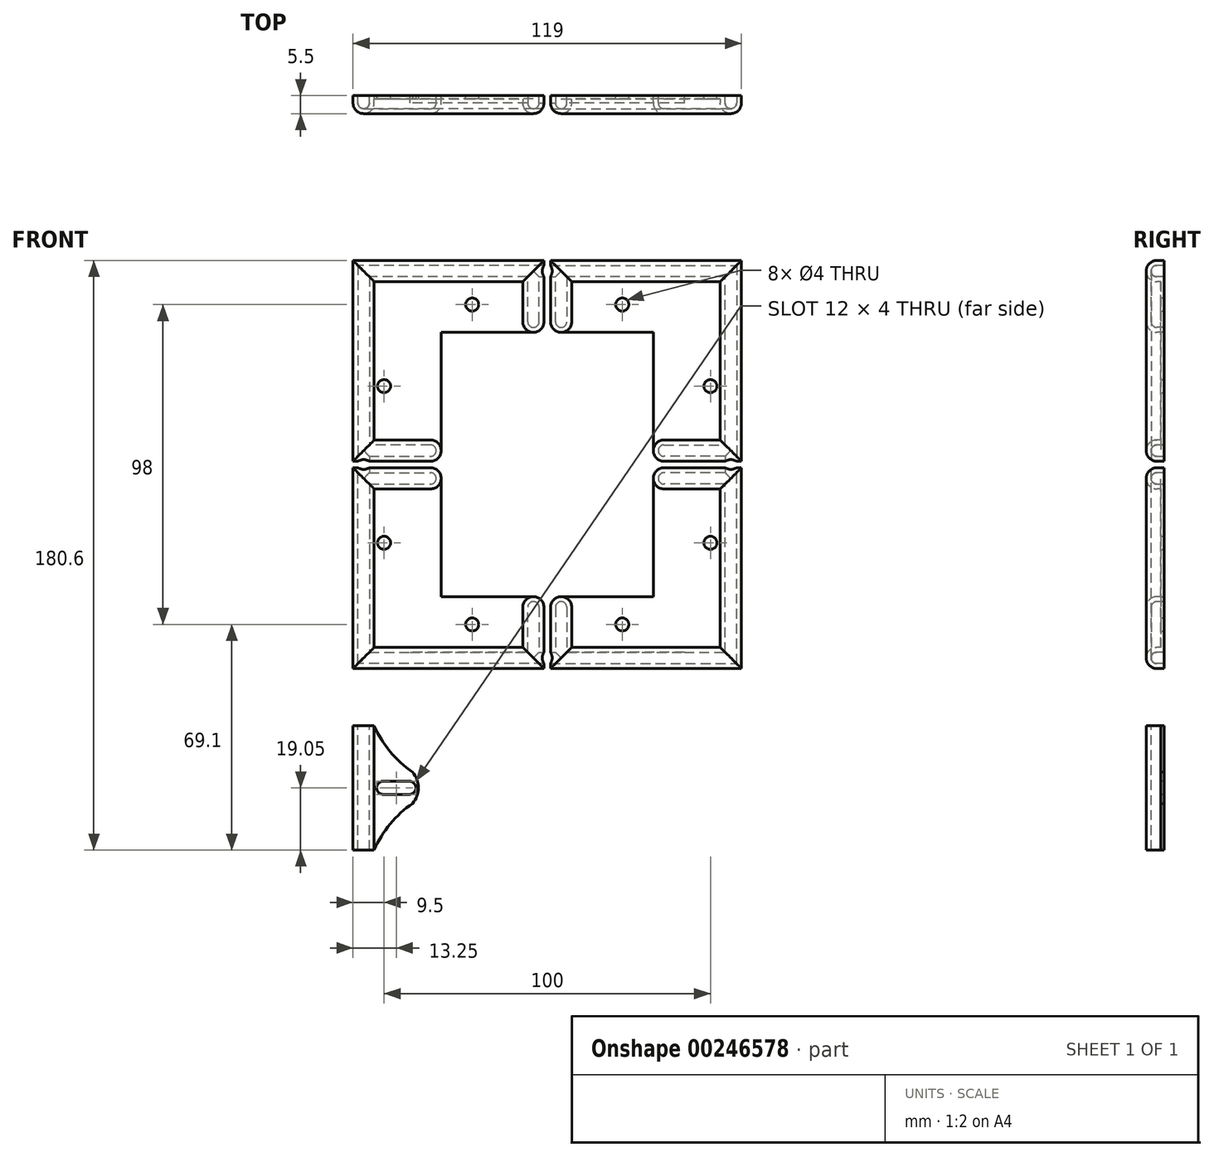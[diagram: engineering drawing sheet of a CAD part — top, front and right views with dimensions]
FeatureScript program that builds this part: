
annotation { "Feature Type Name" : "Feature", "Feature Type Description" : "" }
export const myFeature = defineFeature(function(context is Context, id is Id, definition is map)
    precondition{}
    {
        {
            var Q0;
            Q0=qCreatedBy(makeId("Front.planeOp"),FACE);
            var sketch = newSketch(context, id + "F0", { "sketchPlane" : qUnion([Q0])});
            skLineSegment(sketch, "E0", {"start": v(59.5, 0) * mm, "end": v(59.5, 61.5) * mm});
            skLineSegment(sketch, "E1", {"start": v(59.5, 61.5) * mm, "end": v(1, 61.5) * mm});
            skLineSegment(sketch, "E2", {"start": v(1, 61.5) * mm, "end": v(1, 39.5) * mm});
            skLineSegment(sketch, "E3", {"start": v(1, 39.5) * mm, "end": v(32.5, 39.5) * mm});
            skLineSegment(sketch, "E4", {"start": v(32.5, 39.5) * mm, "end": v(32.5, 0) * mm});
            skLineSegment(sketch, "E5", {"start": v(32.5, 0) * mm, "end": v(59.5, 0) * mm});
            skCircle(sketch, "E6", {"center": v(23, 48) * mm, "radius": 2 * mm});
            skCircle(sketch, "E7", {"center": v(50, 23) * mm, "radius": 2 * mm});
            skSolve(sketch);
        }
        {
            var Q0;
            Q0=qCreatedBy(makeId("Right.planeOp"),FACE);
            var sketch = newSketch(context, id + "F1", { "sketchPlane" : qUnion([Q0])});
            skArc(sketch, "E8", {"start": v(-2.25, 61.5) * mm, "mid": v(-5.5, 58.25) * mm, "end": v(-2.25, 55) * mm});
            skLineSegment(sketch, "E9", {"start": v(0, 61.5) * mm, "end": v(-2.25, 61.5) * mm});
            skLineSegment(sketch, "E10", {"start": v(-2.25, 55) * mm, "end": v(0, 55) * mm});
            skPoint(sketch, "E11", {"position": v(-5.5, 58.25) * mm});
            skLineSegment(sketch, "E12", {"start": v(0, 55) * mm, "end": v(0, 61.5) * mm});
            skSolve(sketch);
        }
        {
            var Q0;
            Q0=qCreatedBy(makeId("Top.planeOp"),FACE);
            cPlane(context, id + "F2", {"entities" : qUnion([Q0]), "cplaneType" : CPlaneType.OFFSET, "offset" : 39.5 * mm, "width" : 150 * mm, "height" : 150 * mm});
        }
        {
            var Q0;
            Q0=qCreatedBy(id+"F2.planeOp",FACE);
            var sketch = newSketch(context, id + "F3", { "sketchPlane" : qUnion([Q0])});
            skArc(sketch, "E13", {"start": v(1, -2.25) * mm, "mid": v(4.25, -5.5) * mm, "end": v(7.5, -2.25) * mm});
            skPoint(sketch, "E14", {"position": v(4.25, -5.5) * mm});
            skPoint(sketch, "E15", {"position": v(1, -2.25) * mm});
            skLineSegment(sketch, "E16", {"start": v(1, 0) * mm, "end": v(7.5, 0) * mm});
            skLineSegment(sketch, "E17", {"start": v(7.5, -2.25) * mm, "end": v(7.5, 0) * mm});
            skLineSegment(sketch, "E18", {"start": v(1, -2.25) * mm, "end": v(1, 0) * mm});
            skSolve(sketch);
        }
        {
            var Q0;
            Q0=makeQuery(id+"F3.imprint","IMPRINT",FACE,{"disambiguationData":[TD([[makeQuery(id+"F3.imprint","IMPRINT",EDGE,{"derivedFrom":sQuery(id+"F3.wireOp",EDGE,"E13")}),1.0]])]});
            var Q1;
            Q1=sQuery(id+"F0.wireOp",EDGE,"E2");
            var Q2;
            Q2=sQuery(id+"F0.wireOp",EDGE,"E1");
            var Q3;
            Q3=sQuery(id+"F0.wireOp",EDGE,"E0");
            var Q4;
            Q4=sQuery(id+"F0.wireOp",EDGE,"E5");
            sweep(context, id + "F4", {"profiles" : qUnion([Q0]), "path" : qUnion([Q1, Q2, Q3, Q4])});
        }
        {
            var Q0;
            Q0=qSketchRegion(id+"F0",true);
            extrude(context, id + "F5", {"entities" : qUnion([Q0]), "operationType" : NewBodyOperationType.ADD, "depth" : 1 * mm});
        }
        {
            var Q0;
            Q0=makeQuery(id+"F4.opSweep","CAP_EDGE",EDGE,{"disambiguationData":[OSD([sQuery(id+"F0.wireOp",VERTEX,"E2.end"),sQuery(id+"F3.wireOp",EDGE,"E13")])],"isStart":true});
            var Q1;
            Q1=makeQuery(id+"F4.opSweep","CAP_EDGE",EDGE,{"disambiguationData":[OSD([sQuery(id+"F0.wireOp",VERTEX,"E5.start"),sQuery(id+"F3.wireOp",EDGE,"E13")])],"isStart":false});
            fillet(context, id + "F6", {"entities" : qUnion([Q0, Q1]), "radius" : 3.25 * mm, "tangentPropagation" : true, "allowEdgeOverflow" : false});
        }
        {
            var Q0;
            Q0=makeQuery(id+"F4.opSweep","SWEPT_BODY",BODY,{"disambiguationData":[OSD([sQuery(id+"F0.wireOp",EDGE,"E5"),sQuery(id+"F3.wireOp",EDGE,"E13"),sQuery(id+"F3.wireOp",EDGE,"gyNzIB6L-VOB3-YhDV-Oq0C-YqyF9qzvM0NL"),sQuery(id+"F3.wireOp",EDGE,"E16"),sQuery(id+"F3.wireOp",EDGE,"E17")])]});
            var Q1;
            Q1=qCreatedBy(makeId("Right.planeOp"),FACE);
            mirror(context, id + "F7", {"entities" : qUnion([Q0]), "mirrorPlane" : qUnion([Q1])});
        }
        {
            var Q0;
            Q0=qCreatedBy(makeId("Top.planeOp"),FACE);
            cPlane(context, id + "F8", {"entities" : qUnion([Q0]), "cplaneType" : CPlaneType.OFFSET, "offset" : 1 * mm, "oppositeDirection" : true, "width" : 150 * mm, "height" : 150 * mm});
        }
        {
            var Q0;
            Q0=makeQuery(id+"F4.opSweep","SWEPT_BODY",BODY,{"disambiguationData":[OSD([sQuery(id+"F0.wireOp",EDGE,"E5"),sQuery(id+"F3.wireOp",EDGE,"E13"),sQuery(id+"F3.wireOp",EDGE,"E16"),sQuery(id+"F3.wireOp",EDGE,"E17"),sQuery(id+"F3.wireOp",EDGE,"E18")])]});
            var Q1;
            Q1=makeQuery(id+"F7.opPattern","COPY",BODY,{"derivedFrom":makeQuery(id+"F4.opSweep","SWEPT_BODY",BODY,{"disambiguationData":[OSD([sQuery(id+"F0.wireOp",EDGE,"E5"),sQuery(id+"F3.wireOp",EDGE,"E13"),sQuery(id+"F3.wireOp",EDGE,"E16"),sQuery(id+"F3.wireOp",EDGE,"E17"),sQuery(id+"F3.wireOp",EDGE,"E18")])]}),"instanceName":"1"});
            var Q2;
            Q2=qCreatedBy(id+"F8.planeOp",FACE);
            mirror(context, id + "F9", {"entities" : qUnion([Q0, Q1]), "mirrorPlane" : qUnion([Q2])});
        }
        {
            var Q0;
            {var subQ0=sQuery(id+"F0.wireOp",EDGE,"E2");Q0=makeQuery(id+"F7.opPattern","COPY",FACE,{"derivedFrom":makeQuery(id+"F5.boolean.opBoolean","MERGE",FACE,{"derivedFrom":[makeQuery(id+"F4.opSweep","SWEPT_FACE",FACE,{"disambiguationData":[OSD([subQ0,sQuery(id+"F3.wireOp",EDGE,"E16")])]}),makeQuery(id+"F5.opExtrude","CAP_FACE",FACE,{"disambiguationData":[OSD([sQuery(id+"F0.wireOp",EDGE,"E0"),sQuery(id+"F0.wireOp",EDGE,"E1"),subQ0,sQuery(id+"F0.wireOp",EDGE,"E3"),sQuery(id+"F0.wireOp",EDGE,"E4"),sQuery(id+"F0.wireOp",EDGE,"E5"),sQuery(id+"F0.wireOp",EDGE,"E6"),sQuery(id+"F0.wireOp",EDGE,"E7")])],"isStart":true})]}),"instanceName":"1"});}
            var Q1;
            {var subQ0=sQuery(id+"F0.wireOp",EDGE,"E2");Q1=makeQuery(id+"F9.opPattern","COPY",FACE,{"derivedFrom":makeQuery(id+"F7.opPattern","COPY",FACE,{"derivedFrom":makeQuery(id+"F5.boolean.opBoolean","MERGE",FACE,{"derivedFrom":[makeQuery(id+"F4.opSweep","SWEPT_FACE",FACE,{"disambiguationData":[OSD([subQ0,sQuery(id+"F3.wireOp",EDGE,"E16")])]}),makeQuery(id+"F5.opExtrude","CAP_FACE",FACE,{"disambiguationData":[OSD([sQuery(id+"F0.wireOp",EDGE,"E0"),sQuery(id+"F0.wireOp",EDGE,"E1"),subQ0,sQuery(id+"F0.wireOp",EDGE,"E3"),sQuery(id+"F0.wireOp",EDGE,"E4"),sQuery(id+"F0.wireOp",EDGE,"E5"),sQuery(id+"F0.wireOp",EDGE,"E6"),sQuery(id+"F0.wireOp",EDGE,"E7")])],"isStart":true})]}),"instanceName":"1"}),"instanceName":"1"});}
            var Q2;
            {var subQ0=sQuery(id+"F0.wireOp",EDGE,"E2");Q2=makeQuery(id+"F9.opPattern","COPY",FACE,{"derivedFrom":makeQuery(id+"F5.boolean.opBoolean","MERGE",FACE,{"derivedFrom":[makeQuery(id+"F4.opSweep","SWEPT_FACE",FACE,{"disambiguationData":[OSD([subQ0,sQuery(id+"F3.wireOp",EDGE,"E16")])]}),makeQuery(id+"F5.opExtrude","CAP_FACE",FACE,{"disambiguationData":[OSD([sQuery(id+"F0.wireOp",EDGE,"E0"),sQuery(id+"F0.wireOp",EDGE,"E1"),subQ0,sQuery(id+"F0.wireOp",EDGE,"E3"),sQuery(id+"F0.wireOp",EDGE,"E4"),sQuery(id+"F0.wireOp",EDGE,"E5"),sQuery(id+"F0.wireOp",EDGE,"E6"),sQuery(id+"F0.wireOp",EDGE,"E7")])],"isStart":true})]}),"instanceName":"1"});}
            var Q3;
            {var subQ0=sQuery(id+"F0.wireOp",EDGE,"E2");Q3=makeQuery(id+"F5.boolean.opBoolean","MERGE",FACE,{"derivedFrom":[makeQuery(id+"F4.opSweep","SWEPT_FACE",FACE,{"disambiguationData":[OSD([subQ0,sQuery(id+"F3.wireOp",EDGE,"E16")])]}),makeQuery(id+"F5.opExtrude","CAP_FACE",FACE,{"disambiguationData":[OSD([sQuery(id+"F0.wireOp",EDGE,"E0"),sQuery(id+"F0.wireOp",EDGE,"E1"),subQ0,sQuery(id+"F0.wireOp",EDGE,"E3"),sQuery(id+"F0.wireOp",EDGE,"E4"),sQuery(id+"F0.wireOp",EDGE,"E5"),sQuery(id+"F0.wireOp",EDGE,"E6"),sQuery(id+"F0.wireOp",EDGE,"E7")])],"isStart":true})]});}
            shell(context, id + "F10", {"entities" : qUnion([Q0, Q1, Q2, Q3]), "thickness" : 1.5 * mm});
        }
        {
            var Q0;
            Q0=qCreatedBy(makeId("Right.planeOp"),FACE);
            var sketch = newSketch(context, id + "F11", { "sketchPlane" : qUnion([Q0])});
            skArc(sketch, "E19.0.1", {"start": v(-2.25, 56.5) * mm, "mid": v(-3.49, 57.01) * mm, "end": v(-4, 58.25) * mm});
            skArc(sketch, "E19.0.2", {"start": v(-4, 58.25) * mm, "mid": v(-3.49, 59.49) * mm, "end": v(-2.25, 60) * mm});
            skArc(sketch, "E19.0.4", {"start": v(-2.25, 60) * mm, "mid": v(-3.49, 59.49) * mm, "end": v(-4, 58.25) * mm});
            skArc(sketch, "E19.0.5", {"start": v(-4, 58.25) * mm, "mid": v(-3.49, 57.01) * mm, "end": v(-2.25, 56.5) * mm});
            skArc(sketch, "E20", {"start": v(-2.25, 56.5) * mm, "mid": v(-4, 58.25) * mm, "end": v(-2.25, 60) * mm});
            skLineSegment(sketch, "E21.bottom", {"start": v(-2.25, 56.5) * mm, "end": v(0, 56.5) * mm});
            skLineSegment(sketch, "E21.top", {"start": v(-2.25, 60) * mm, "end": v(0, 60) * mm});
            skLineSegment(sketch, "E21.right", {"start": v(0, 56.5) * mm, "end": v(0, 60) * mm});
            skArc(sketch, "E22.0.1", {"start": v(-2.25, -58.5) * mm, "mid": v(-3.49, -59.01) * mm, "end": v(-4, -60.25) * mm});
            skArc(sketch, "E22.0.2", {"start": v(-4, -60.25) * mm, "mid": v(-3.49, -61.49) * mm, "end": v(-2.25, -62) * mm});
            skArc(sketch, "E22.0.4", {"start": v(-4, -60.25) * mm, "mid": v(-3.49, -61.49) * mm, "end": v(-2.25, -62) * mm});
            skArc(sketch, "E22.0.5", {"start": v(-2.25, -58.5) * mm, "mid": v(-3.49, -59.01) * mm, "end": v(-4, -60.25) * mm});
            skArc(sketch, "E23", {"start": v(-2.25, -58.5) * mm, "mid": v(-4, -60.25) * mm, "end": v(-2.25, -62) * mm});
            skLineSegment(sketch, "E24.0", {"start": v(0, -44.75) * mm, "end": v(0, -62) * mm});
            skLineSegment(sketch, "E25.bottom", {"start": v(-2.25, -62) * mm, "end": v(0, -62) * mm});
            skLineSegment(sketch, "E25.top", {"start": v(-2.25, -58.5) * mm, "end": v(0, -58.5) * mm});
            skLineSegment(sketch, "E25.right", {"start": v(0, -62) * mm, "end": v(0, -58.5) * mm});
            skLineSegment(sketch, "E26.trimOffspring", {"start": v(-2.25, -58.5) * mm, "end": v(-2.25, -58.5) * mm});
            skSolve(sketch);
        }
        {
            var Q0;
            Q0=qSketchRegion(id+"F11",true);
            extrude(context, id + "F12", {"entities" : qUnion([Q0]), "operationType" : NewBodyOperationType.REMOVE, "endBound" : BoundingType.SYMMETRIC, "oppositeDirection" : true, "depth" : 84 * mm});
        }
        {
            var Q0;
            Q0=qCreatedBy(makeId("Top.planeOp"),FACE);
            var sketch = newSketch(context, id + "F13", { "sketchPlane" : qUnion([Q0])});
            skArc(sketch, "E27.0.1", {"start": v(58, -2.25) * mm, "mid": v(57.49, -3.49) * mm, "end": v(56.25, -4) * mm});
            skArc(sketch, "E27.0.2", {"start": v(56.25, -4) * mm, "mid": v(55.01, -3.49) * mm, "end": v(54.5, -2.25) * mm});
            skArc(sketch, "E27.0.5", {"start": v(54.5, -2.25) * mm, "mid": v(55.01, -3.49) * mm, "end": v(56.25, -4) * mm});
            skArc(sketch, "E27.0.6", {"start": v(56.25, -4) * mm, "mid": v(57.49, -3.49) * mm, "end": v(58, -2.25) * mm});
            skArc(sketch, "E28.0.0", {"start": v(-54.5, -2.25) * mm, "mid": v(-55.01, -3.49) * mm, "end": v(-56.25, -4) * mm});
            skArc(sketch, "E28.0.1", {"start": v(-56.25, -4) * mm, "mid": v(-57.49, -3.49) * mm, "end": v(-58, -2.25) * mm});
            skArc(sketch, "E28.0.4", {"start": v(-56.25, -4) * mm, "mid": v(-57.49, -3.49) * mm, "end": v(-58, -2.25) * mm});
            skArc(sketch, "E28.0.5", {"start": v(-54.5, -2.25) * mm, "mid": v(-55.01, -3.49) * mm, "end": v(-56.25, -4) * mm});
            skArc(sketch, "E29", {"start": v(58, -2.25) * mm, "mid": v(56.25, -4) * mm, "end": v(54.5, -2.25) * mm});
            skLineSegment(sketch, "E30", {"start": v(54.5, -2.25) * mm, "end": v(54.5, 0) * mm});
            skLineSegment(sketch, "E31", {"start": v(54.5, 0) * mm, "end": v(58, 0) * mm});
            skLineSegment(sketch, "E32", {"start": v(58, 0) * mm, "end": v(58, -2.25) * mm});
            skArc(sketch, "E33.MirrorCS", {"start": v(-58, -2.25) * mm, "mid": v(-57.49, -3.49) * mm, "end": v(-56.25, -4) * mm});
            skArc(sketch, "E34.MirrorCS", {"start": v(-56.25, -4) * mm, "mid": v(-55.01, -3.49) * mm, "end": v(-54.5, -2.25) * mm});
            skLineSegment(sketch, "E35.MirrorCS", {"start": v(-54.5, -2.25) * mm, "end": v(-54.5, 0) * mm});
            skArc(sketch, "E36.MirrorCS", {"start": v(-58, -2.25) * mm, "mid": v(-56.25, -4) * mm, "end": v(-54.5, -2.25) * mm});
            skLineSegment(sketch, "E37.MirrorCS", {"start": v(-54.5, 0) * mm, "end": v(-58, 0) * mm});
            skLineSegment(sketch, "E38.MirrorCS", {"start": v(-58, 0) * mm, "end": v(-58, -2.25) * mm});
            skSolve(sketch);
        }
        {
            var Q0;
            Q0=qSketchRegion(id+"F13",true);
            extrude(context, id + "F14", {"entities" : qUnion([Q0]), "operationType" : NewBodyOperationType.REMOVE, "endBound" : BoundingType.SYMMETRIC, "depth" : 70 * mm});
        }
        {
            var Q0;
            Q0=qCreatedBy(id+"F8.planeOp",FACE);
            cPlane(context, id + "F15", {"entities" : qUnion([Q0]), "cplaneType" : CPlaneType.OFFSET, "offset" : 80 * mm, "oppositeDirection" : true, "width" : 150 * mm, "height" : 150 * mm});
        }
        {
            var Q0;
            Q0=qCreatedBy(id+"F15.planeOp",FACE);
            var sketch = newSketch(context, id + "F16", { "sketchPlane" : qUnion([Q0])});
            skLineSegment(sketch, "E39.0.2", {"start": v(-59.5, 0) * mm, "end": v(-59.5, -2.25) * mm});
            skLineSegment(sketch, "E39.0.3", {"start": v(-59.5, 0) * mm, "end": v(-58, 0) * mm});
            skArc(sketch, "E40.0.1", {"start": v(-54.5, -2.25) * mm, "mid": v(-56.25, -4) * mm, "end": v(-58, -2.25) * mm});
            skArc(sketch, "E40.0.3", {"start": v(-54.5, -2.25) * mm, "mid": v(-55.01, -3.49) * mm, "end": v(-56.25, -4) * mm});
            skArc(sketch, "E40.0.4", {"start": v(-54.5, -2.25) * mm, "mid": v(-55.01, -3.49) * mm, "end": v(-56.25, -4) * mm});
            skArc(sketch, "E40.0.6", {"start": v(-54.5, -2.25) * mm, "mid": v(-55.01, -3.49) * mm, "end": v(-56.25, -4) * mm});
            skArc(sketch, "E40.0.7", {"start": v(-56.25, -4) * mm, "mid": v(-57.49, -3.49) * mm, "end": v(-58, -2.25) * mm});
            skArc(sketch, "E41.0.1", {"start": v(-53, -2.25) * mm, "mid": v(-56.25, -5.5) * mm, "end": v(-59.5, -2.25) * mm});
            skArc(sketch, "E41.0.3", {"start": v(-53, -2.25) * mm, "mid": v(-56.25, -5.5) * mm, "end": v(-59.5, -2.25) * mm});
            skLineSegment(sketch, "E42.0.2", {"start": v(-39.5, -1) * mm, "end": v(-53, -1) * mm});
            skLineSegment(sketch, "E43", {"start": v(-54.5, -2.25) * mm, "end": v(-54.5, -1) * mm});
            skLineSegment(sketch, "E44", {"start": v(-58, -2.25) * mm, "end": v(-58, 0) * mm});
            skLineSegment(sketch, "E45", {"start": v(-53, -2.25) * mm, "end": v(-53, -1) * mm});
            skLineSegment(sketch, "E46", {"start": v(-54.5, -1) * mm, "end": v(-54.5, 0) * mm});
            skLineSegment(sketch, "E47.trimOffspring", {"start": v(-54.5, 0) * mm, "end": v(-39.5, 0) * mm});
            skLineSegment(sketch, "E48", {"start": v(-39.5, -1) * mm, "end": v(-39.5, 0) * mm});
            skSolve(sketch);
        }
        {
            var Q0;
            Q0=makeQuery(id+"F16.imprint","IMPRINT",FACE,{"disambiguationData":[TD([[makeQuery(id+"F16.imprint","IMPRINT",EDGE,{"derivedFrom":sQuery(id+"F16.wireOp",EDGE,"E39.0.2")}),1.0]])]});
            extrude(context, id + "F17", {"entities" : qUnion([Q0]), "oppositeDirection" : true, "depth" : 38.1 * mm});
        }
        {
            var Q0;
            Q0=makeQuery(id+"F17.opExtrude","SWEPT_FACE",FACE,{"disambiguationData":[OSD([sQuery(id+"F16.wireOp",EDGE,"E42.0.2")])]});
            var sketch = newSketch(context, id + "F18", { "sketchPlane" : qUnion([Q0])});
            skLineSegment(sketch, "E49.0.0", {"start": v(-39.5, -81) * mm, "end": v(-53, -81) * mm});
            skLineSegment(sketch, "E49.0.1", {"start": v(-53, -81) * mm, "end": v(-53, -119.1) * mm});
            skLineSegment(sketch, "E49.0.2", {"start": v(-53, -119.1) * mm, "end": v(-39.5, -119.1) * mm});
            skLineSegment(sketch, "E49.0.3", {"start": v(-39.5, -119.1) * mm, "end": v(-39.5, -81) * mm});
            skLineSegment(sketch, "E50.0.0", {"start": v(-53, -81) * mm, "end": v(-59.5, -81) * mm});
            skLineSegment(sketch, "E50.0.1", {"start": v(-59.5, -81) * mm, "end": v(-59.5, -119.1) * mm});
            skLineSegment(sketch, "E50.0.2", {"start": v(-59.5, -119.1) * mm, "end": v(-53, -119.1) * mm});
            skLineSegment(sketch, "E50.0.3", {"start": v(-53, -119.1) * mm, "end": v(-53, -81) * mm});
            skArc(sketch, "E51", {"start": v(-41.22, -104.82) * mm, "mid": v(-39.5, -100.05) * mm, "end": v(-41.22, -95.28) * mm});
            skPoint(sketch, "E51.centerSnap0", {"position": v(-39.5, -100.05) * mm});
            skArc(sketch, "E52", {"start": v(-41.22, -104.82) * mm, "mid": v(-48.12, -111.13) * mm, "end": v(-53, -119.1) * mm});
            skLineSegment(sketch, "E53", {"start": v(-39.5, -100.05) * mm, "end": v(-74.37, -100.05) * mm, "construction": true});
            skArc(sketch, "E54.MirrorCS", {"start": v(-41.22, -95.28) * mm, "mid": v(-48.12, -88.97) * mm, "end": v(-53, -81) * mm});
            skLineSegment(sketch, "E55.0.0", {"start": v(-32.5, -41.5) * mm, "end": v(-32.5, -5.25) * mm});
            skArc(sketch, "E55.0.1", {"start": v(-32.5, -5.25) * mm, "mid": v(-33.45, -7.55) * mm, "end": v(-35.75, -8.5) * mm});
            skLineSegment(sketch, "E55.0.2", {"start": v(-35.75, -8.5) * mm, "end": v(-53, -8.5) * mm});
            skLineSegment(sketch, "E55.0.3", {"start": v(-53, -8.5) * mm, "end": v(-53, -57) * mm});
            skLineSegment(sketch, "E55.0.4", {"start": v(-53, -57) * mm, "end": v(-7.5, -57) * mm});
            skLineSegment(sketch, "E55.0.5", {"start": v(-7.5, -57) * mm, "end": v(-7.5, -44.75) * mm});
            skArc(sketch, "E55.0.6", {"start": v(-7.5, -44.75) * mm, "mid": v(-6.55, -42.45) * mm, "end": v(-4.25, -41.5) * mm});
            skLineSegment(sketch, "E55.0.7", {"start": v(-4.25, -41.5) * mm, "end": v(-32.5, -41.5) * mm});
            skArc(sketch, "E56", {"start": v(-50.25, -98.05) * mm, "mid": v(-52.25, -100.05) * mm, "end": v(-50.25, -102.05) * mm});
            skArc(sketch, "E57", {"start": v(-42.25, -102.05) * mm, "mid": v(-40.25, -100.05) * mm, "end": v(-42.25, -98.05) * mm});
            skLineSegment(sketch, "E58", {"start": v(-50.25, -98.05) * mm, "end": v(-42.25, -98.05) * mm});
            skLineSegment(sketch, "E59", {"start": v(-42.25, -102.05) * mm, "end": v(-50.25, -102.05) * mm});
            skPoint(sketch, "E60", {"position": v(-46.25, -81) * mm});
            skPoint(sketch, "E61", {"position": v(-46.25, -98.05) * mm});
            skSolve(sketch);
        }
        {
            var Q0;
            {var subQ0=sQuery(id+"F18.wireOp",EDGE,"E49.0.0");Q0=makeQuery(id+"F18.imprint","IMPRINT",FACE,{"disambiguationData":[TD([[makeQuery(id+"F18.imprint","IMPRINT",EDGE,{"derivedFrom":subQ0}),1.0]])]});}
            var Q1;
            {var subQ0=sQuery(id+"F18.wireOp",EDGE,"E49.0.2");Q1=makeQuery(id+"F18.imprint","IMPRINT",FACE,{"disambiguationData":[TD([[makeQuery(id+"F18.imprint","IMPRINT",EDGE,{"derivedFrom":subQ0}),-1.0]])]});}
            var Q2;
            Q2=makeQuery(id+"F18.imprint","IMPRINT",FACE,{"disambiguationData":[TD([[makeQuery(id+"F18.imprint","IMPRINT",EDGE,{"derivedFrom":sQuery(id+"F18.wireOp",EDGE,"E56")}),1.0]])]});
            extrude(context, id + "F19", {"entities" : qUnion([Q0, Q1, Q2]), "operationType" : NewBodyOperationType.REMOVE, "endBound" : BoundingType.UP_TO_NEXT, "oppositeDirection" : true, "depth" : 25 * mm});
        }
    });
